# Revit family: BC_Hitachi_RAS-3HVNC1_LOD400
name_source: partatom
category: Equipement de génie climatique
revit_build: Autodesk Revit 2017 (Build: 20160225_1515(x64)
units: mm (PartAtom-declared; Revit-internal decimal feet)

## family parameters
Basée sur le plan de construction = Non
Cote de connecteur circulaire = Utiliser le diamètre
Couper avec des vides une fois chargée = Non
Numéro OmniClass = 23.75.00.00
Partagée = Non
Point de calcul de pièce = Non
Titre OmniClass = Climate Control (HVAC)
Toujours verticalement = Oui
Type d'élément = Normal

## types (1)
- RAS-3HVNC1
    BC_OBJECT_ID = 29466
    BC_OBJECT_VERSION = #1
    BC_VARIANT_ID = 192672
    Coefficient of Performance (COP) = 4
    Commentaires du type = RAS-3HVNC1
    Compressor Type = Scroll DC Inverter driven
    Cooling Capacity = 7100 W
    Cooling Capacity Max = 8000 W
    Cooling Capacity Min = 3200 W
    Cooling Running Current = 9 A
    Cooling Sound Pressure Level = 48
    Energy efficiency ratio (EER) = 3.14
    Frequency = 50 Hz
    Gas Diameter = 15.88 mm
    Heating Capacity = 8000 W
    Heating Capacity Max = 10600 W
    Heating Capacity Min = 3500 W
    Heating Running Current = 8 A
    Heating Sound Pressure Level = 50
    Height difference between OU & IU (higher OU) = 30000.00 mm
    Height difference between OU & IU (lower OU) = 20000.00 mm
    Liquid Diameter = 9.52 mm
    Manufacturer = Hitachi Air Conditioning Europe SAS
    Material = IVX Material
    Maximum chargless piping length = 20.00 mm
    Maximum connectable indoor units = 2
    Maximum connected capacity = 110 %
    Maximum piping length (additional refrigerant needed) = 50 m (40g/m)
    Miminum piping length = 5000.00 mm
    Minimum connectable indoor units = 1
    Minimum connected capacity = 90 %
    Modèle = IVX - RAS-3HVNC1
    Net Weight = 44.00 kg
    Nominal Air Flow = 2682.0 m³/h
    Nominal Voltage = 230 V
    Number of Poles = 1
    Overall Depth = 300.00 mm
    Overall Height = 800.00 mm
    Overall Width = 792.00 mm
    Recommended circuit breaker = 20 A
    Reference = RAS-3HVNC1
    Refrigerant Type = R410A
    Refrigerant charge before shipment = 1.90 kg
    Size of power cable (according to EN 60335-1) = 3 x 4.0 mm²
    Size of transmission cable between indoor unit and outdoor unit = 2 x 0.75 mm²
    Sound level = 66
    Sound pressure level Night mode cooling (dB(A)) = 46
    Starting current (A) = Less than maximum current
    Wired Remote control model (Optional) = PC-ARFPE

## geometry (parser evidence)
native form markers: Blend x4
no freeform markers — native parametric forms only
